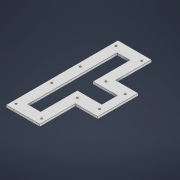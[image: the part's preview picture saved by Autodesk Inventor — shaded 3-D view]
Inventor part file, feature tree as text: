
AUTODESK INVENTOR PART (.ipt)
format: ipt  version: 2021 (Build 250183000, 183)  size: 384,000 bytes
history: native  units: mm
features: extrude x5, sketch x4, projected_geometry x1
ambient origin geometry x8: Origin, YZ Plane, XZ Plane, XY Plane, X Axis, Y Axis, Z Axis, Center Point
bodies: Volumenkörper1 (feature_tree)
feature tree (10):
  extrude  "Extrusion1"  Depth=200.0mm
  extrude  "Extrusion3"  Depth=2.0mm
  extrude  "Extrusion2"  Depth=10.5mm
  extrude  "Extrusion4"  Depth=2.0mm
  extrude  "Extrusion5"  Depth=2.0mm
  sketch  "Skizze1"  dims[d0=60.0mm d1=200.0mm]
  sketch  "Skizze3"  dims[d2=2.0mm d3=0.0mm d4=3.2mm]
  sketch  "Skizze4"  dims[d5=3.2mm d6=10.5mm]
  projected_geometry  "Projizierte Kontur1"
  sketch  "Skizze5"  dims[d7=10.5mm d8=23.0mm d9=23.0mm d10=3.2mm d11=3.2mm d12=23.0mm d13=23.0mm d14=25.5mm d15=25.5mm d16=5.0mm d17=5.0mm d19=4.0mm d20=5.0mm d23=4.0mm d24=4.0mm d25=4.0mm d26=4.0mm d27=4.0mm d28=4.0mm d29=4.0mm d30=4.0mm d31=4.0mm d32=4.0mm d33=4.0mm d34=4.0mm d35=4.0mm d36=4.0mm d37=4.0mm d38=4.0mm d39=4.0mm d40=4.0mm d41=4.0mm d42=4.0mm d43=4.0mm d44=4.0mm d45=4.0mm d48=12.6mm d49=12.6mm d50=12.6mm d51=12.6mm d52=12.6mm d53=12.6mm d54=2.0mm d55=0.0mm d56=40.0mm d57=0.0mm d58=3.2mm d59=3.2mm d60=23.0mm d61=23.0mm d64=37.0mm d65=37.0mm d66=4.0mm d67=4.0mm d68=4.0mm d69=4.0mm d70=4.0mm d71=4.0mm d72=4.0mm d73=4.0mm d74=4.0mm d75=4.0mm d76=4.0mm d77=15.6mm d78=15.6mm d79=2.0mm d80=0.0mm d81=10.0mm d82=10.0mm d83=8.0mm d84=8.0mm d85=15.0mm d86=10.0mm d87=10.0mm d88=18.6mm d89=18.6mm d90=2.0mm d91=0.0mm]
